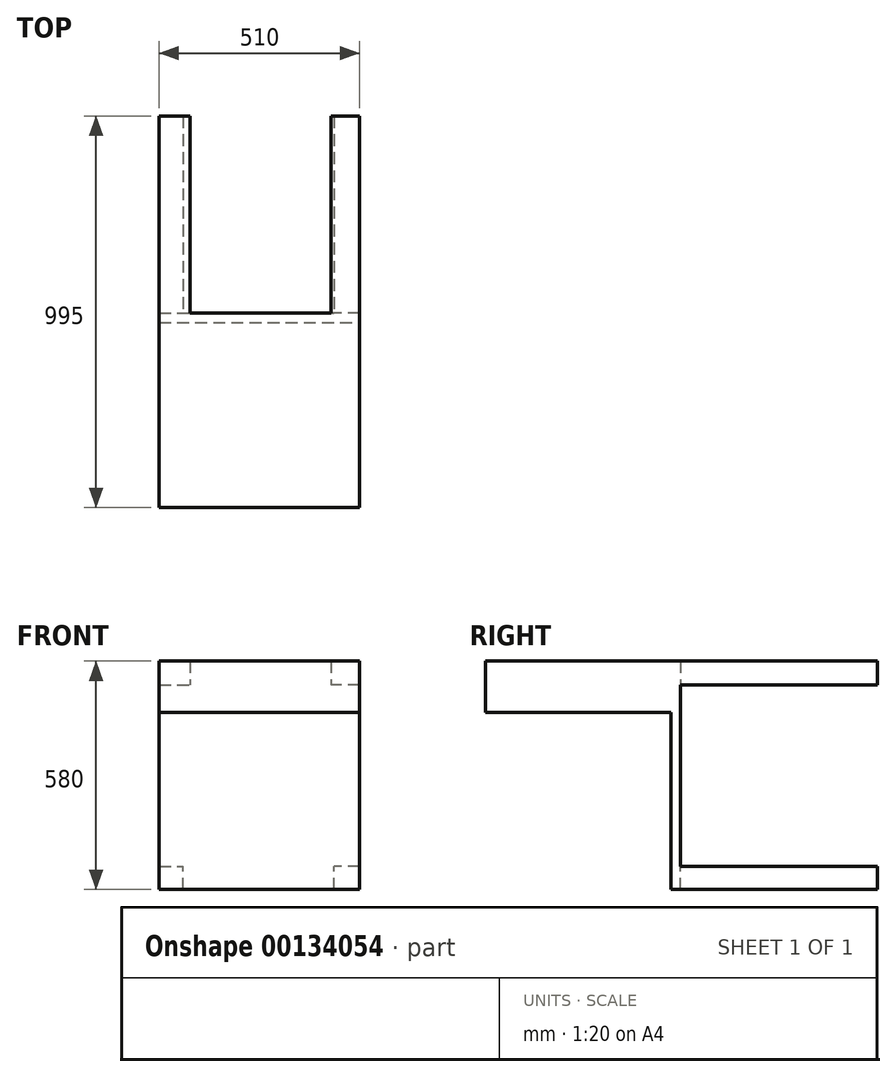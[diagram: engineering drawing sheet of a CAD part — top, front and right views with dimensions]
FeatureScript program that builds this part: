
annotation { "Feature Type Name" : "Feature", "Feature Type Description" : "" }
export const myFeature = defineFeature(function(context is Context, id is Id, definition is map)
    precondition{}
    {
        {
            var Q0;
            Q0=qCreatedBy(makeId("Front.planeOp"),FACE);
            var sketch = newSketch(context, id + "F0", { "sketchPlane" : qUnion([Q0])});
            skLineSegment(sketch, "E0.bottom", {"start": v(-266.22, 396.2) * mm, "end": v(243.78, 396.2) * mm});
            skLineSegment(sketch, "E0.top", {"start": v(-266.22, -183.8) * mm, "end": v(243.78, -183.8) * mm});
            skLineSegment(sketch, "E0.left", {"start": v(-266.22, 396.2) * mm, "end": v(-266.22, -183.8) * mm});
            skLineSegment(sketch, "E0.right", {"start": v(243.78, 396.2) * mm, "end": v(243.78, -183.8) * mm});
            skSolve(sketch);
        }
        {
            var Q0;
            Q0=makeQuery(id+"F0.imprint","IMPRINT",FACE,{"disambiguationData":[TD([[makeQuery(id+"F0.imprint","IMPRINT",EDGE,{"derivedFrom":sQuery(id+"F0.wireOp",EDGE,"E0.bottom")}),-1.0]])]});
            extrude(context, id + "F1", {"entities" : qUnion([Q0]), "depth" : 25 * mm});
        }
        {
            var Q0;
            Q0=makeQuery(id+"F1.opExtrude","CAP_FACE",FACE,{"disambiguationData":[OSD([sQuery(id+"F0.wireOp",EDGE,"E0.bottom"),sQuery(id+"F0.wireOp",EDGE,"E0.top"),sQuery(id+"F0.wireOp",EDGE,"E0.left"),sQuery(id+"F0.wireOp",EDGE,"E0.right")])],"isStart":false});
            var sketch = newSketch(context, id + "F2", { "sketchPlane" : qUnion([Q0])});
            skLineSegment(sketch, "E1.bottom", {"start": v(-266.22, 396.2) * mm, "end": v(243.78, 396.2) * mm});
            skLineSegment(sketch, "E1.top", {"start": v(-266.22, 266.2) * mm, "end": v(243.78, 266.2) * mm});
            skLineSegment(sketch, "E1.left", {"start": v(-266.22, 396.2) * mm, "end": v(-266.22, 266.2) * mm});
            skLineSegment(sketch, "E1.right", {"start": v(243.78, 396.2) * mm, "end": v(243.78, 266.2) * mm});
            skSolve(sketch);
        }
        {
            var Q0;
            Q0=makeQuery(id+"F2.imprint","IMPRINT",FACE,{"disambiguationData":[TD([[makeQuery(id+"F2.imprint","IMPRINT",EDGE,{"derivedFrom":sQuery(id+"F2.wireOp",EDGE,"E1.bottom")}),-1.0]])]});
            extrude(context, id + "F3", {"entities" : qUnion([Q0]), "operationType" : NewBodyOperationType.ADD, "depth" : 470 * mm});
        }
        {
            var Q0;
            Q0=makeQuery(id+"F1.opExtrude","CAP_FACE",FACE,{"disambiguationData":[OSD([sQuery(id+"F0.wireOp",EDGE,"E0.bottom"),sQuery(id+"F0.wireOp",EDGE,"E0.top"),sQuery(id+"F0.wireOp",EDGE,"E0.left"),sQuery(id+"F0.wireOp",EDGE,"E0.right")])],"isStart":true});
            var sketch = newSketch(context, id + "F4", { "sketchPlane" : qUnion([Q0])});
            skLineSegment(sketch, "E2.bottom", {"start": v(-243.78, 396.2) * mm, "end": v(-170.78, 396.2) * mm});
            skLineSegment(sketch, "E2.top", {"start": v(-243.78, 335.39) * mm, "end": v(-170.78, 335.39) * mm});
            skLineSegment(sketch, "E2.left", {"start": v(-243.78, 396.2) * mm, "end": v(-243.78, 335.39) * mm});
            skLineSegment(sketch, "E2.right", {"start": v(-170.78, 396.2) * mm, "end": v(-170.78, 335.39) * mm});
            skLineSegment(sketch, "E3.bottom", {"start": v(266.22, 396.2) * mm, "end": v(186.95, 396.2) * mm});
            skLineSegment(sketch, "E3.top", {"start": v(266.22, 335.39) * mm, "end": v(186.95, 335.39) * mm});
            skLineSegment(sketch, "E3.left", {"start": v(266.22, 396.2) * mm, "end": v(266.22, 335.39) * mm});
            skLineSegment(sketch, "E3.right", {"start": v(186.95, 396.2) * mm, "end": v(186.95, 335.39) * mm});
            skLineSegment(sketch, "E4.bottom", {"start": v(-243.78, -183.8) * mm, "end": v(-178.15, -183.8) * mm});
            skLineSegment(sketch, "E4.top", {"start": v(-243.78, -124.63) * mm, "end": v(-178.15, -124.63) * mm});
            skLineSegment(sketch, "E4.left", {"start": v(-243.78, -183.8) * mm, "end": v(-243.78, -124.63) * mm});
            skLineSegment(sketch, "E4.right", {"start": v(-178.15, -183.8) * mm, "end": v(-178.15, -124.63) * mm});
            skLineSegment(sketch, "E5.bottom", {"start": v(266.22, -183.8) * mm, "end": v(205.14, -183.8) * mm});
            skLineSegment(sketch, "E5.top", {"start": v(266.22, -124.63) * mm, "end": v(205.14, -124.63) * mm});
            skLineSegment(sketch, "E5.left", {"start": v(266.22, -183.8) * mm, "end": v(266.22, -124.63) * mm});
            skLineSegment(sketch, "E5.right", {"start": v(205.14, -183.8) * mm, "end": v(205.14, -124.63) * mm});
            skSolve(sketch);
        }
        {
            var Q0;
            Q0=makeQuery(id+"F4.imprint","IMPRINT",FACE,{"disambiguationData":[TD([[makeQuery(id+"F4.imprint","IMPRINT",EDGE,{"derivedFrom":sQuery(id+"F4.wireOp",EDGE,"E2.bottom")}),1.0]])]});
            var Q1;
            Q1=makeQuery(id+"F4.imprint","IMPRINT",FACE,{"disambiguationData":[TD([[makeQuery(id+"F4.imprint","IMPRINT",EDGE,{"derivedFrom":sQuery(id+"F4.wireOp",EDGE,"E3.bottom")}),1.0]])]});
            var Q2;
            Q2=makeQuery(id+"F4.imprint","IMPRINT",FACE,{"disambiguationData":[TD([[makeQuery(id+"F4.imprint","IMPRINT",EDGE,{"derivedFrom":sQuery(id+"F4.wireOp",EDGE,"E4.bottom")}),-1.0]])]});
            var Q3;
            Q3=makeQuery(id+"F4.imprint","IMPRINT",FACE,{"disambiguationData":[TD([[makeQuery(id+"F4.imprint","IMPRINT",EDGE,{"derivedFrom":sQuery(id+"F4.wireOp",EDGE,"E5.bottom")}),-1.0]])]});
            extrude(context, id + "F5", {"entities" : qUnion([Q0, Q1, Q2, Q3]), "operationType" : NewBodyOperationType.ADD, "depth" : 500 * mm});
        }
    });
